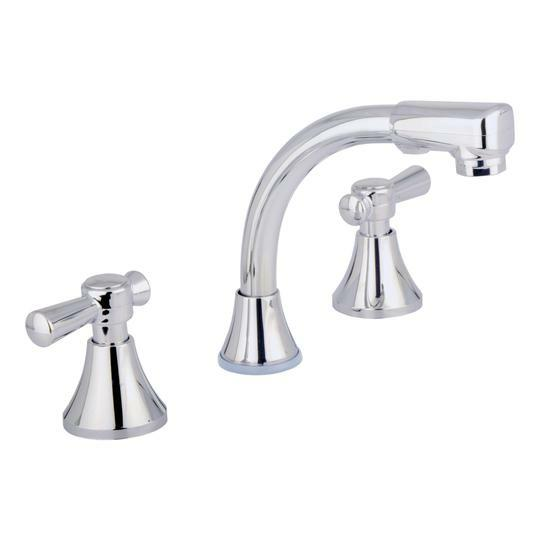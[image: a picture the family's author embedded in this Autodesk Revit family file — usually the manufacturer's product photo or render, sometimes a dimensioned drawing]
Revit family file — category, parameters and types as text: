
# Revit family: 01-1403-11 MEZCLADOR LAVAMANOS 8”-4” TOSCANA
name_source: partatom
category: Plumbing Fixtures
revit_build: Autodesk Revit 2018 (Build: 20170223_1515(x64)
units: mm (PartAtom-declared; Revit-internal decimal feet)

## family parameters
Cut with Voids When Loaded = No
Host = Face
OmniClass Number = 23.31.11.00
Part Type = Normal
Room Calculation Point = No
Round Connector Dimension = Use Diameter
Shared = No

## types (1)
- 01-1403-11
    Alto = 166.7 mm  [stored 0.546916 ft]
    Alto Aireador = 135.5 mm
    Ancho brazo = 138.8 mm  [stored 0.455381 ft]
    Ancho entre manijas = 203.2 mm  [stored 0.666667 ft]
    Ancho manija = 70 mm
    CW Connection = Yes
    Default Elevation = 0 mm  [stored 0 ft]
    Description = Bimando
    HW Connection = Yes
    Link Ficha Tecnica = http://infotecnica.gricol.com
    Manufacturer = Gricol
    Model = 01-1403-11
    Plastico - ABS Cromado = Plastico - ABS Cromado
    Product Name = MEZCLADOR LAVAMANOS 8”-4” TOSCANA
    Type Image = MEZCLADOR LAVAMANOS 8”-4” TOSCANA.jpg
    URL = https://www.gricol.com
    Vent Connection = No
    Waste Connection = No

note: [stored X ft] marks values corroborated as IEEE doubles in the binary element streams (Revit-internal decimal feet)

## geometry (parser evidence)
native form markers: Blend x2, Sweep x2
no freeform markers — native parametric forms only
